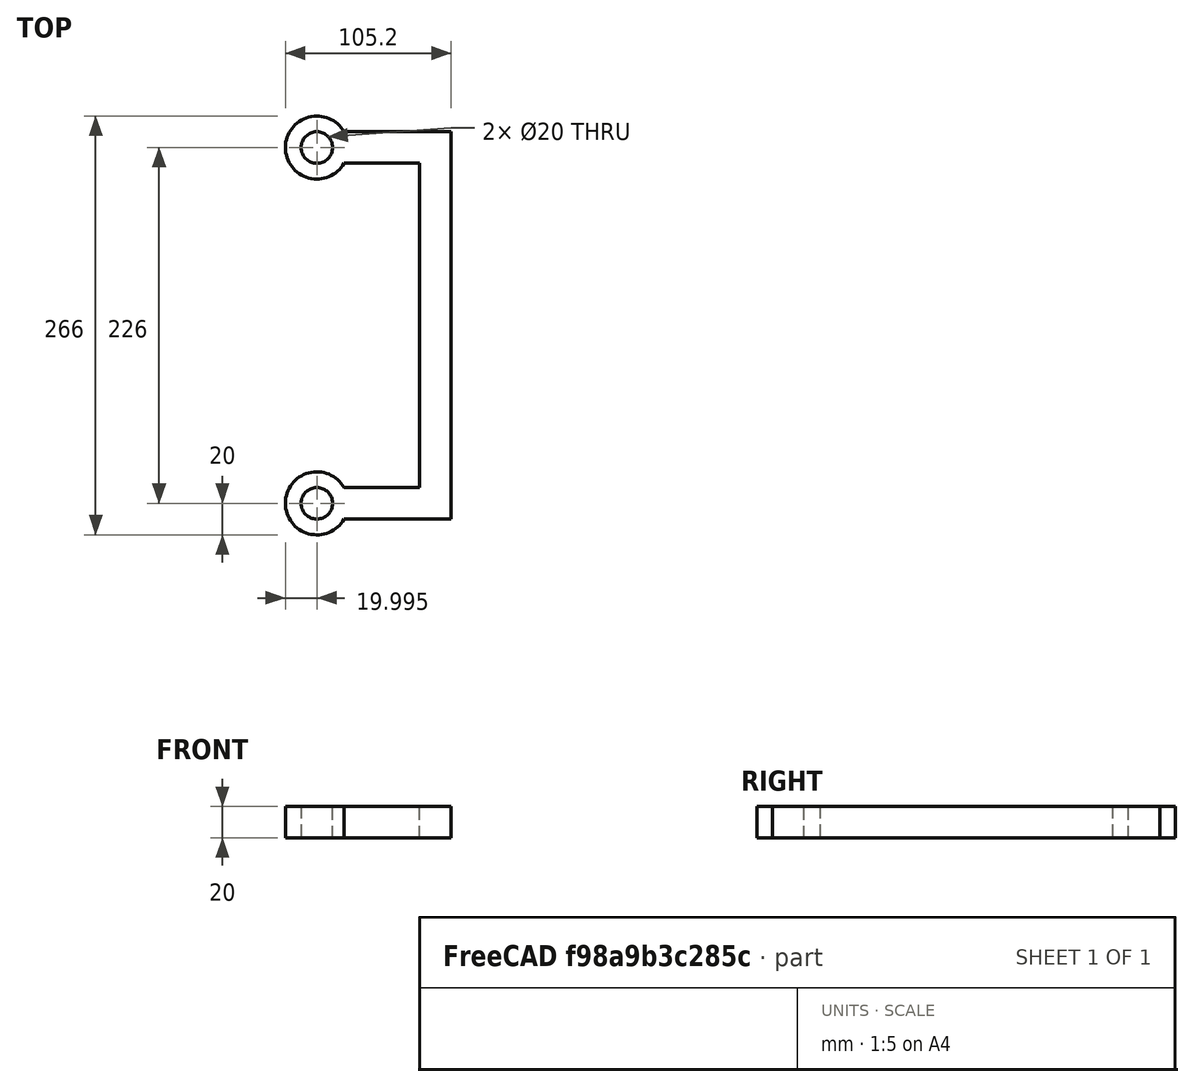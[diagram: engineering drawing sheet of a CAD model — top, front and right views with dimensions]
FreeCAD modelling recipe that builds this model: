
FCSTD DOCUMENT  (FreeCAD 0.20R29177 +426 (Git))
Label: rotary-branch-1
License: All rights reserved
LicenseURL: http://en.wikipedia.org/wiki/All_rights_reserved
objects: Sketcher::SketchObject×1, PartDesign::Body×1, Part::Extrusion×1
note: 3 computed .brp shape members not serialized (recipe doc carries the construction recipe); baked Part::Feature solids carry a one-line shape summary decoded from their .brp

FEATURE [Sketcher::SketchObject] Sketch
  FullyConstrained = false
  MapMode = 5
  Support = -> [XY_Plane]
  sketch-geometry (15):
    g0: LineSegment StartX=12.1156 StartY=0 StartZ=0 EndX=60 EndY=0 EndZ=0
    g1: LineSegment StartX=60 StartY=206 StartZ=0 EndX=60 EndY=0 EndZ=0
    g2: LineSegment StartX=60 StartY=206 StartZ=0 EndX=12.1156 EndY=206 EndZ=0
    g3: LineSegment StartX=12.1156 StartY=226 StartZ=0 EndX=80 EndY=226 EndZ=0
    g4: LineSegment StartX=80 StartY=226 StartZ=0 EndX=80 EndY=-20 EndZ=0
    g5: LineSegment StartX=80 StartY=-20 StartZ=0 EndX=12.1156 EndY=-20 EndZ=0
    g6: LineSegment StartX=60 StartY=206 StartZ=0 EndX=60 EndY=226 EndZ=0
    g7: LineSegment StartX=60 StartY=206 StartZ=0 EndX=80 EndY=206 EndZ=0
    g8: ArcOfCircle CenterX=-5.20491 CenterY=-10 CenterZ=0 NormalX=0 NormalY=0 NormalZ=1 AngleXU=0 Radius=20 StartAngle=0.523599 EndAngle=5.75959
    g9: LineSegment StartX=0 StartY=0 StartZ=0 EndX=-5.20491 EndY=-10 EndZ=0
    g10: LineSegment StartX=-5.20491 StartY=-10 StartZ=0 EndX=0 EndY=-20 EndZ=0
    g11: Circle CenterX=-5.20491 CenterY=-10 CenterZ=0 NormalX=0 NormalY=0 NormalZ=1 AngleXU=0 Radius=10
    g12: LineSegment StartX=-5.20491 StartY=-10 StartZ=0 EndX=-5.20491 EndY=216 EndZ=0
    g13: ArcOfCircle CenterX=-5.20491 CenterY=216 CenterZ=0 NormalX=0 NormalY=0 NormalZ=1 AngleXU=0 Radius=20 StartAngle=0.523599 EndAngle=5.75959
    g14: Circle CenterX=-5.20491 CenterY=216 CenterZ=0 NormalX=0 NormalY=0 NormalZ=1 AngleXU=0 Radius=10
  constraints (37):
    c: PointOnObject(g0,g-1)
    c: Coincident(g1,g0)
    c: Vertical(g1)
    c: Coincident(g2,g1)
    c: Horizontal(g2)
    c: DistanceY(g1,g1) = 206
    c: Horizontal(g3)
    c: Coincident(g4,g3)
    c: Vertical(g4)
    c: Coincident(g5,g4)
    c: PointOnObject(g10,g-2)
    c: Horizontal(g5)
    c: Coincident(g6,g1)
    c: PointOnObject(g6,g3)
    c: Vertical(g6)
    c: Coincident(g7,g1)
    c: PointOnObject(g7,g4)
    c: Horizontal(g7)
    c: Equal(g6,g7)
    c: Coincident(g9,g-1)
    c: Coincident(g9,g8)
    c: Coincident(g10,g8)
    c: Equal(g10,g9)
    c: Coincident(g11,g8)
    c: Diameter(g11) = 20
    c: Diameter(g8) = 40
    c: Coincident(g8,g0)
    c: Coincident(g5,g8)
    c: DistanceX(g8) = -5.20491
    c: DistanceY(g8) = -10
    c: Coincident(g12,g8)
    c: Vertical(g12)
    c: Equal(g13,g8)
    c: Coincident(g3,g13)
    c: Coincident(g2,g13)
    c: Coincident(g14,g13)
    c: Diameter(g14) = 20
FEATURE [PartDesign::Body] Body
  Group = -> [Sketch]
  Origin = -> Origin
FEATURE [Part::Extrusion] Extrude
  Base = -> Sketch
  Dir = (0,0,1)
  DirMode = 2
  FaceMakerClass = Part::FaceMakerBullseye
  LengthFwd = 20
  LengthRev = 0
  Solid = true
  Symmetric = false
